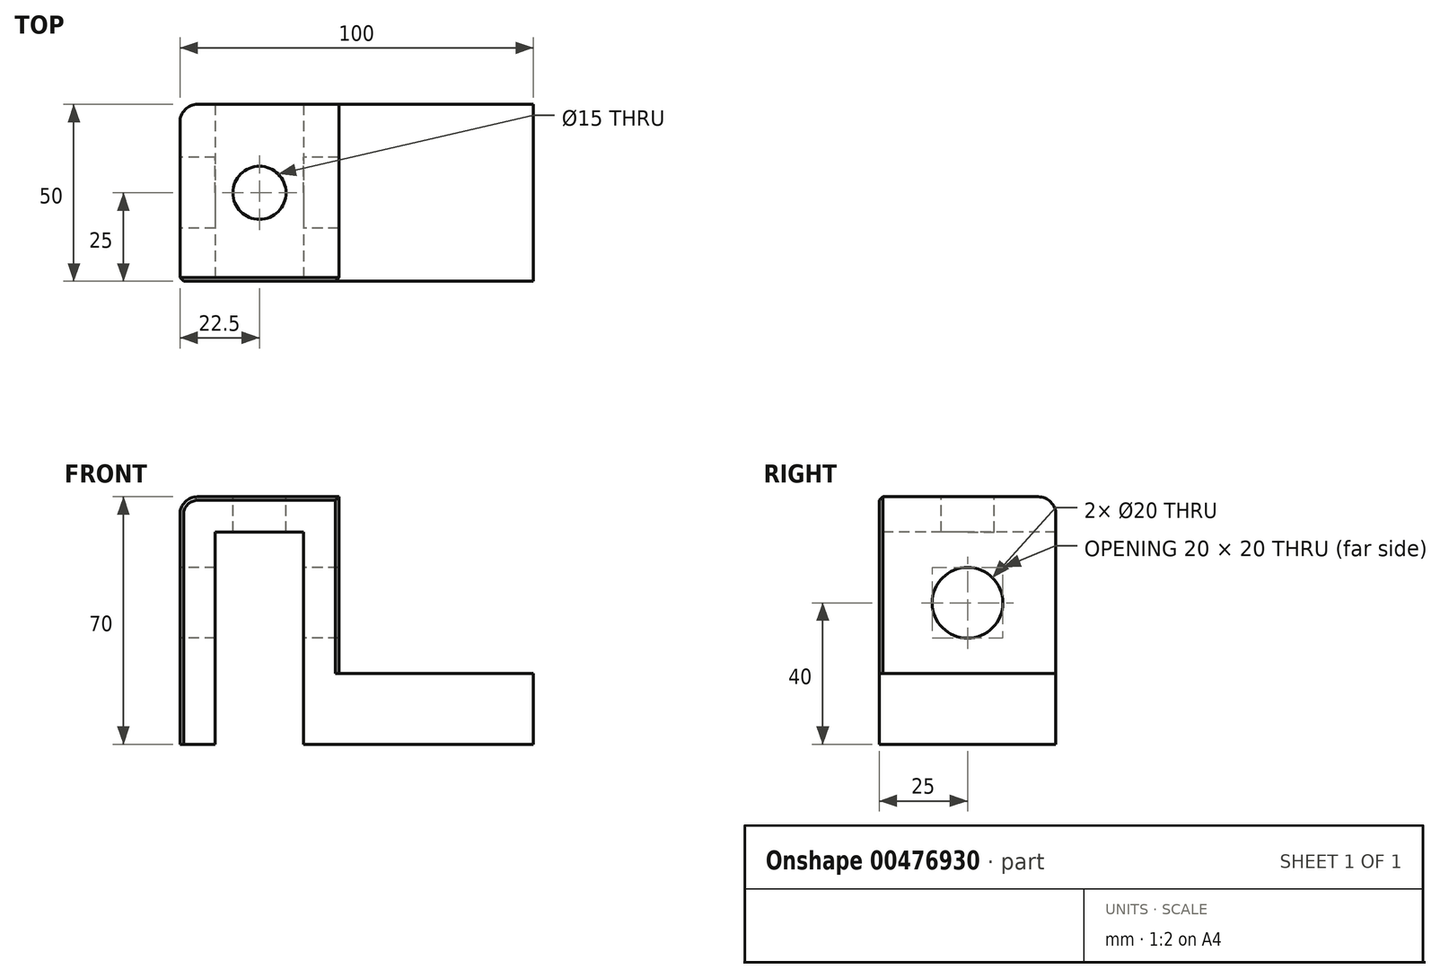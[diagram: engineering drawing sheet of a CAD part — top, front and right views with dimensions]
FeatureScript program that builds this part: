
annotation { "Feature Type Name" : "Feature", "Feature Type Description" : "" }
export const myFeature = defineFeature(function(context is Context, id is Id, definition is map)
    precondition{}
    {
        {
            var Q0;
            Q0=qCreatedBy(makeId("Top.planeOp"),FACE);
            var sketch = newSketch(context, id + "F0", { "sketchPlane" : qUnion([Q0])});
            skLineSegment(sketch, "E0.bottom", {"start": v(0, 0) * mm, "end": v(100, 0) * mm});
            skLineSegment(sketch, "E0.top", {"start": v(0, 50) * mm, "end": v(100, 50) * mm});
            skLineSegment(sketch, "E0.left", {"start": v(0, 0) * mm, "end": v(0, 50) * mm});
            skLineSegment(sketch, "E0.right", {"start": v(100, 0) * mm, "end": v(100, 50) * mm});
            skSolve(sketch);
        }
        {
            var Q0;
            Q0 = qSketchRegion(id + "F0", true);
            extrude(context, id + "F1", {"entities" : qUnion([Q0]), "depth" : 20 * mm});
        }
        {
            var Q0;
            Q0=makeQuery(id+"F1.opExtrude","CAP_FACE",FACE,{"disambiguationData":[OSD([sQuery(id+"F0.wireOp",EDGE,"E0.bottom"),sQuery(id+"F0.wireOp",EDGE,"E0.top"),sQuery(id+"F0.wireOp",EDGE,"E0.left"),sQuery(id+"F0.wireOp",EDGE,"E0.right")])],"isStart":false});
            var sketch = newSketch(context, id + "F2", { "sketchPlane" : qUnion([Q0])});
            skLineSegment(sketch, "E1.bottom", {"start": v(0, 0) * mm, "end": v(45, 0) * mm});
            skLineSegment(sketch, "E1.top", {"start": v(0, 50) * mm, "end": v(45, 50) * mm});
            skLineSegment(sketch, "E1.left", {"start": v(0, 0) * mm, "end": v(0, 50) * mm});
            skLineSegment(sketch, "E1.right", {"start": v(45, 0) * mm, "end": v(45, 50) * mm});
            skSolve(sketch);
        }
        {
            var Q0;
            Q0 = qSketchRegion(id + "F2", true);
            extrude(context, id + "F3", {"entities" : qUnion([Q0]), "operationType" : NewBodyOperationType.ADD, "depth" : 50 * mm});
        }
        {
            var Q0;
            Q0=makeQuery(id+"F3.boolean.opBoolean","MERGE",FACE,{"derivedFrom":[makeQuery(id+"F1.opExtrude","SWEPT_FACE",FACE,{"disambiguationData":[OSD([sQuery(id+"F0.wireOp",EDGE,"E0.bottom")])]}),makeQuery(id+"F3.opExtrude","SWEPT_FACE",FACE,{"disambiguationData":[OSD([sQuery(id+"F2.wireOp",EDGE,"E1.bottom")])]})]});
            var sketch = newSketch(context, id + "F4", { "sketchPlane" : qUnion([Q0])});
            skLineSegment(sketch, "E2.bottom", {"start": v(10, 0) * mm, "end": v(35, 0) * mm});
            skLineSegment(sketch, "E2.top", {"start": v(10, 60) * mm, "end": v(35, 60) * mm});
            skLineSegment(sketch, "E2.left", {"start": v(10, 0) * mm, "end": v(10, 60) * mm});
            skLineSegment(sketch, "E2.right", {"start": v(35, 0) * mm, "end": v(35, 60) * mm});
            skSolve(sketch);
        }
        {
            var Q0;
            Q0 = qSketchRegion(id + "F4", true);
            var Q1;
            Q1=makeQuery(id+"F3.boolean.opBoolean","MERGE",FACE,{"derivedFrom":[makeQuery(id+"F1.opExtrude","SWEPT_FACE",FACE,{"disambiguationData":[OSD([sQuery(id+"F0.wireOp",EDGE,"E0.top")])]}),makeQuery(id+"F3.opExtrude","SWEPT_FACE",FACE,{"disambiguationData":[OSD([sQuery(id+"F2.wireOp",EDGE,"E1.top")])]})]});
            extrude(context, id + "F5", {"entities" : qUnion([Q0]), "operationType" : NewBodyOperationType.REMOVE, "endBound" : BoundingType.UP_TO_SURFACE, "oppositeDirection" : true, "endBoundEntityFace" : qUnion([Q1]), "depth" : 35.7 * mm});
        }
        {
            var Q0;
            Q0=makeQuery(id+"F3.boolean.opBoolean","MERGE",FACE,{"derivedFrom":[makeQuery(id+"F1.opExtrude","SWEPT_FACE",FACE,{"disambiguationData":[OSD([sQuery(id+"F0.wireOp",EDGE,"E0.left")])]}),makeQuery(id+"F3.opExtrude","SWEPT_FACE",FACE,{"disambiguationData":[OSD([sQuery(id+"F2.wireOp",EDGE,"E1.left")])]})]});
            var sketch = newSketch(context, id + "F6", { "sketchPlane" : qUnion([Q0])});
            skCircle(sketch, "E3", {"center": v(-25, 40) * mm, "radius": 10 * mm});
            skSolve(sketch);
        }
        {
            var Q0;
            Q0 = qSketchRegion(id + "F6", true);
            var Q1;
            Q1=makeQuery(id+"F3.opExtrude","SWEPT_FACE",FACE,{"disambiguationData":[OSD([sQuery(id+"F2.wireOp",EDGE,"E1.right")])]});
            extrude(context, id + "F7", {"entities" : qUnion([Q0]), "operationType" : NewBodyOperationType.REMOVE, "endBound" : BoundingType.UP_TO_SURFACE, "oppositeDirection" : true, "endBoundEntityFace" : qUnion([Q1]), "depth" : 25 * mm});
        }
        {
            var Q0;
            Q0=makeQuery(id+"F3.opExtrude","CAP_FACE",FACE,{"disambiguationData":[OSD([sQuery(id+"F2.wireOp",EDGE,"E1.bottom"),sQuery(id+"F2.wireOp",EDGE,"E1.top"),sQuery(id+"F2.wireOp",EDGE,"E1.left"),sQuery(id+"F2.wireOp",EDGE,"E1.right")])],"isStart":false});
            var sketch = newSketch(context, id + "F8", { "sketchPlane" : qUnion([Q0])});
            skLineSegment(sketch, "E4", {"start": v(45, 0) * mm, "end": v(0, 50) * mm, "construction": true});
            skLineSegment(sketch, "E5", {"start": v(45, 50) * mm, "end": v(0, 0) * mm, "construction": true});
            skCircle(sketch, "E6", {"center": v(22.5, 25) * mm, "radius": 7.5 * mm});
            skSolve(sketch);
        }
        {
            var Q0;
            Q0 = qSketchRegion(id + "F8", true);
            var Q1;
            Q1=makeQuery(id+"F5.boolean.opBoolean","COPY",FACE,{"derivedFrom":makeQuery(id+"F5.opExtrude","SWEPT_FACE",FACE,{"disambiguationData":[OSD([sQuery(id+"F4.wireOp",EDGE,"E2.top")])]})});
            extrude(context, id + "F9", {"entities" : qUnion([Q0]), "operationType" : NewBodyOperationType.REMOVE, "endBound" : BoundingType.UP_TO_NEXT, "oppositeDirection" : true, "endBoundEntityFace" : qUnion([Q1]), "depth" : 25 * mm});
        }
        {
            var Q0;
            Q0=makeQuery(id+"F3.opExtrude","CAP_EDGE",EDGE,{"disambiguationData":[OSD([sQuery(id+"F2.wireOp",EDGE,"E1.left")])],"isStart":false});
            var Q1;
            Q1=makeQuery(id+"F3.boolean.opBoolean","MERGE",EDGE,{"derivedFrom":[makeQuery(id+"F1.opExtrude","SWEPT_EDGE",EDGE,{"disambiguationData":[OSD([sQuery(id+"F0.wireOp",EDGE,"E0.top"),sQuery(id+"F0.wireOp",EDGE,"E0.left")])]}),makeQuery(id+"F3.opExtrude","SWEPT_EDGE",EDGE,{"disambiguationData":[OSD([sQuery(id+"F2.wireOp",EDGE,"E1.top"),sQuery(id+"F2.wireOp",EDGE,"E1.left")])]})]});
            var Q2;
            Q2=makeQuery(id+"F3.opExtrude","CAP_EDGE",EDGE,{"disambiguationData":[OSD([sQuery(id+"F2.wireOp",EDGE,"E1.top")])],"isStart":false});
            fillet(context, id + "F10", {"entities" : qUnion([Q0, Q1, Q2]), "radius" : 5 * mm, "tangentPropagation" : true, "allowEdgeOverflow" : false});
        }
        {
            var Q0;
            Q0=makeQuery(id+"F3.boolean.opBoolean","MERGE",EDGE,{"derivedFrom":[makeQuery(id+"F1.opExtrude","SWEPT_EDGE",EDGE,{"disambiguationData":[OSD([sQuery(id+"F0.wireOp",EDGE,"E0.bottom"),sQuery(id+"F0.wireOp",EDGE,"E0.left")])]}),makeQuery(id+"F3.opExtrude","SWEPT_EDGE",EDGE,{"disambiguationData":[OSD([sQuery(id+"F2.wireOp",EDGE,"E1.bottom"),sQuery(id+"F2.wireOp",EDGE,"E1.left")])]})]});
            var Q1;
            Q1=makeQuery(id+"F3.opExtrude","CAP_EDGE",EDGE,{"disambiguationData":[OSD([sQuery(id+"F2.wireOp",EDGE,"E1.bottom")])],"isStart":false});
            var Q2;
            Q2=makeQuery(id+"F3.opExtrude","SWEPT_EDGE",EDGE,{"disambiguationData":[OSD([sQuery(id+"F0.wireOp",EDGE,"E0.bottom"),sQuery(id+"F2.wireOp",EDGE,"E1.bottom"),sQuery(id+"F2.wireOp",EDGE,"E1.right")])]});
            var Q3;
            Q3=makeQuery(id+"F5.boolean.opBoolean","COPY",EDGE,{"derivedFrom":makeQuery(id+"F5.opExtrude","CAP_EDGE",EDGE,{"disambiguationData":[OSD([sQuery(id+"F4.wireOp",EDGE,"E2.right")])],"isStart":true})});
            var Q4;
            Q4=makeQuery(id+"F5.boolean.opBoolean","COPY",EDGE,{"derivedFrom":makeQuery(id+"F5.opExtrude","CAP_EDGE",EDGE,{"disambiguationData":[OSD([sQuery(id+"F4.wireOp",EDGE,"E2.top")])],"isStart":true})});
            var Q5;
            Q5=makeQuery(id+"F5.boolean.opBoolean","COPY",EDGE,{"derivedFrom":makeQuery(id+"F5.opExtrude","CAP_EDGE",EDGE,{"disambiguationData":[OSD([sQuery(id+"F4.wireOp",EDGE,"E2.left")])],"isStart":true})});
            chamfer(context, id + "F11", {"entities" : qUnion([Q0, Q1, Q2, Q3, Q4, Q5]), "width" : 1 * mm, "tangentPropagation" : true});
        }
    });
